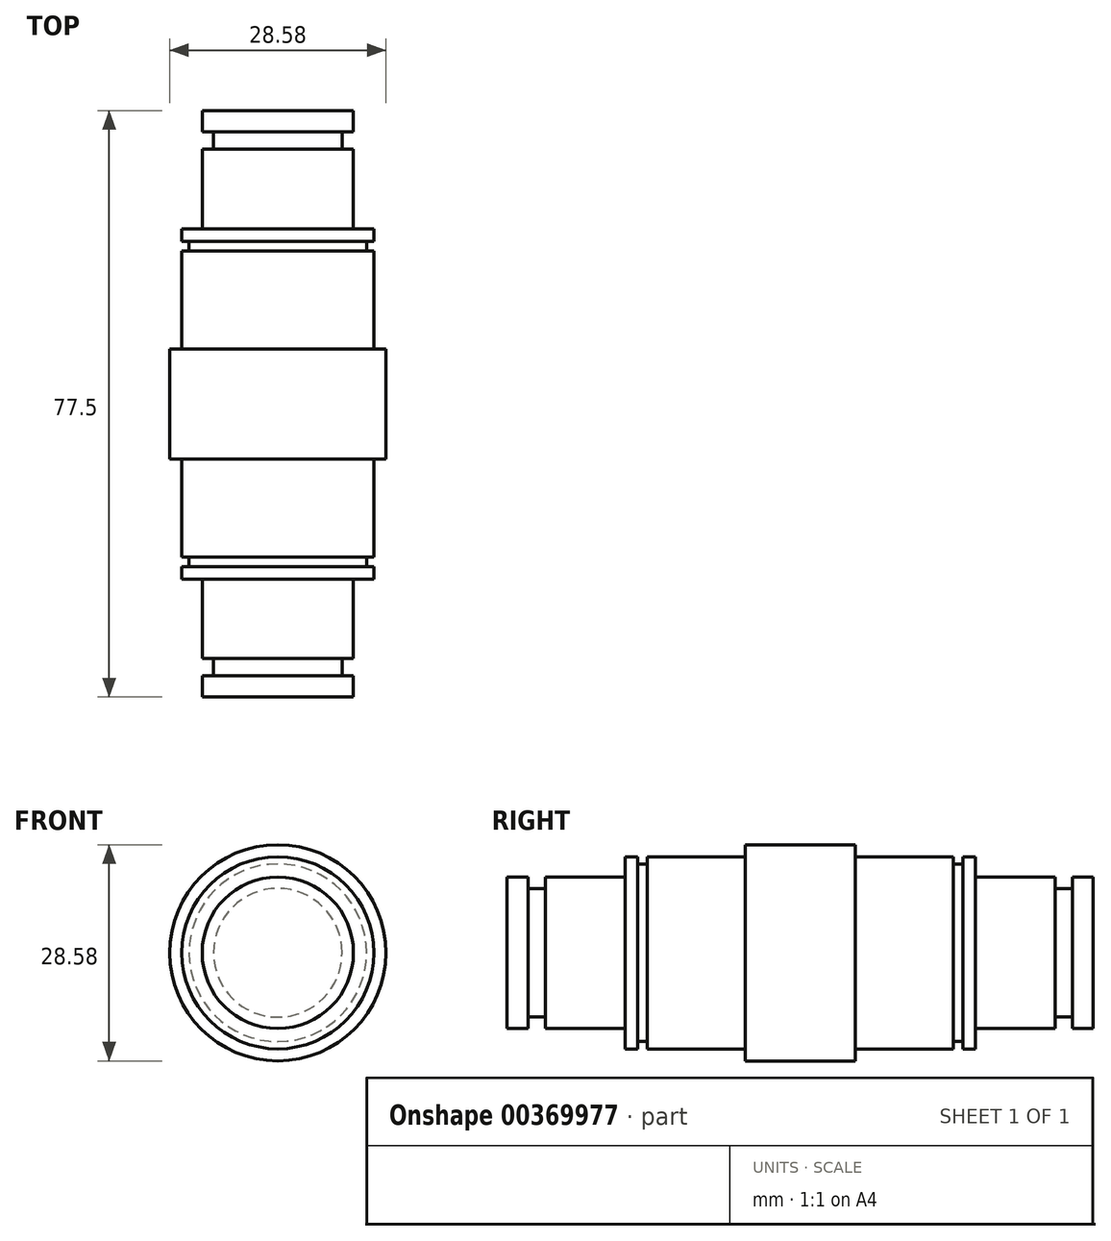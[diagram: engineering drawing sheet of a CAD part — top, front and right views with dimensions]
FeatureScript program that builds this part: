
annotation { "Feature Type Name" : "Feature", "Feature Type Description" : "" }
export const myFeature = defineFeature(function(context is Context, id is Id, definition is map)
    precondition{}
    {
        {
            var Q0;
            Q0=qCreatedBy(makeId("Right.planeOp"),FACE);
            var sketch = newSketch(context, id + "F0", { "sketchPlane" : qUnion([Q0])});
            skLineSegment(sketch, "E0", {"start": v(-30.43, 0) * mm, "end": v(-23.15, 0) * mm, "construction": true});
            skLineSegment(sketch, "E1", {"start": v(0, 0) * mm, "end": v(30.43, 0) * mm, "construction": true});
            skLineSegment(sketch, "E2.bottom", {"start": v(-38.75, 10) * mm, "end": v(-35.96, 10) * mm});
            skLineSegment(sketch, "E3", {"start": v(-38.75, 10) * mm, "end": v(-38.75, 0) * mm});
            skLineSegment(sketch, "E4.bottom", {"start": v(-23.15, 12.7) * mm, "end": v(-21.5, 12.7) * mm});
            skLineSegment(sketch, "E4.left", {"start": v(-23.15, 12.7) * mm, "end": v(-23.15, 10) * mm});
            skLineSegment(sketch, "E4.right", {"start": v(-7.28, 14.29) * mm, "end": v(-7.28, 0) * mm});
            skLineSegment(sketch, "E5.bottom", {"start": v(-7.28, 14.29) * mm, "end": v(0, 14.29) * mm});
            skLineSegment(sketch, "E6.MirrorCS", {"start": v(49.78, 0) * mm, "end": v(0, 0) * mm, "construction": true});
            skLineSegment(sketch, "E7.top", {"start": v(-35.96, 8.5) * mm, "end": v(-33.67, 8.5) * mm});
            skLineSegment(sketch, "E7.left", {"start": v(-35.96, 10) * mm, "end": v(-35.96, 8.5) * mm});
            skLineSegment(sketch, "E7.right", {"start": v(-33.67, 10) * mm, "end": v(-33.67, 8.5) * mm});
            skLineSegment(sketch, "E8.bottom", {"start": v(-21.5, 11.73) * mm, "end": v(-20.23, 11.73) * mm});
            skLineSegment(sketch, "E9", {"start": v(-21.5, 11.73) * mm, "end": v(-21.5, 12.7) * mm});
            skLineSegment(sketch, "E10", {"start": v(-20.23, 11.73) * mm, "end": v(-20.23, 12.7) * mm});
            skLineSegment(sketch, "E11.trimOffspring", {"start": v(-20.23, 12.7) * mm, "end": v(-7.28, 12.7) * mm});
            skLineSegment(sketch, "E12", {"start": v(-38.75, 0) * mm, "end": v(-23.15, 0) * mm});
            skLineSegment(sketch, "E13", {"start": v(-33.67, 10) * mm, "end": v(-23.15, 10) * mm});
            skLineSegment(sketch, "E14", {"start": v(-23.15, 10) * mm, "end": v(-23.15, 0) * mm});
            skLineSegment(sketch, "E15", {"start": v(0, 14.29) * mm, "end": v(0, 0) * mm, "construction": true});
            skLineSegment(sketch, "E16", {"start": v(-7.28, 0) * mm, "end": v(0, 0) * mm});
            skLineSegment(sketch, "E17", {"start": v(-23.15, 0) * mm, "end": v(-7.28, 0) * mm});
            skLineSegment(sketch, "E18.MirrorCS", {"start": v(30.43, 0) * mm, "end": v(23.15, 0) * mm, "construction": true});
            skLineSegment(sketch, "E19.MirrorCS", {"start": v(21.5, 11.73) * mm, "end": v(21.5, 12.7) * mm});
            skLineSegment(sketch, "E20.MirrorCS", {"start": v(35.96, 10) * mm, "end": v(35.96, 8.5) * mm});
            skLineSegment(sketch, "E21.MirrorCS", {"start": v(23.15, 12.7) * mm, "end": v(23.15, 10) * mm});
            skLineSegment(sketch, "E22.MirrorCS", {"start": v(7.28, 14.29) * mm, "end": v(7.28, 0) * mm});
            skLineSegment(sketch, "E23.MirrorCS", {"start": v(7.28, 14.29) * mm, "end": v(0, 14.29) * mm});
            skLineSegment(sketch, "E24.MirrorCS", {"start": v(7.28, 0) * mm, "end": v(0, 0) * mm});
            skLineSegment(sketch, "E25.MirrorCS", {"start": v(33.67, 10) * mm, "end": v(23.15, 10) * mm});
            skLineSegment(sketch, "E26.MirrorCS", {"start": v(38.75, 10) * mm, "end": v(38.75, 0) * mm});
            skLineSegment(sketch, "E27.MirrorCS", {"start": v(23.15, 12.7) * mm, "end": v(21.5, 12.7) * mm});
            skLineSegment(sketch, "E28.MirrorCS", {"start": v(38.75, 0) * mm, "end": v(23.15, 0) * mm});
            skLineSegment(sketch, "E29.MirrorCS", {"start": v(33.67, 10) * mm, "end": v(33.67, 8.5) * mm});
            skLineSegment(sketch, "E30.MirrorCS", {"start": v(20.23, 12.7) * mm, "end": v(7.28, 12.7) * mm});
            skLineSegment(sketch, "E31.MirrorCS", {"start": v(21.5, 11.73) * mm, "end": v(20.23, 11.73) * mm});
            skLineSegment(sketch, "E32.MirrorCS", {"start": v(23.15, 10) * mm, "end": v(23.15, 0) * mm});
            skLineSegment(sketch, "E33.MirrorCS", {"start": v(38.75, 10) * mm, "end": v(35.96, 10) * mm});
            skLineSegment(sketch, "E34.MirrorCS", {"start": v(35.96, 8.5) * mm, "end": v(33.67, 8.5) * mm});
            skLineSegment(sketch, "E35.MirrorCS", {"start": v(23.15, 0) * mm, "end": v(7.28, 0) * mm});
            skLineSegment(sketch, "E36.MirrorCS", {"start": v(20.23, 11.73) * mm, "end": v(20.23, 12.7) * mm});
            skSolve(sketch);
        }
        {
            var Q0;
            Q0=makeQuery(id+"F0.imprint","IMPRINT",FACE,{"disambiguationData":[TD([[makeQuery(id+"F0.imprint","IMPRINT",EDGE,{"derivedFrom":sQuery(id+"F0.wireOp",EDGE,"E4.bottom")}),-1.0]])]});
            var Q1;
            {var subQ1=sQuery(id+"F0.wireOp",EDGE,"E5.bottom");Q1=makeQuery(id+"F0.imprint","IMPRINT",FACE,{"disambiguationData":[TD([[makeQuery(id+"F0.imprint","IMPRINT",EDGE,{"derivedFrom":subQ1}),-1.0]])]});}
            var Q2;
            Q2=makeQuery(id+"F0.imprint","IMPRINT",FACE,{"disambiguationData":[TD([[makeQuery(id+"F0.imprint","IMPRINT",EDGE,{"derivedFrom":sQuery(id+"F0.wireOp",EDGE,"E19.MirrorCS")}),-1.0]])]});
            var Q3;
            Q3=makeQuery(id+"F0.imprint","IMPRINT",FACE,{"disambiguationData":[TD([[makeQuery(id+"F0.imprint","IMPRINT",EDGE,{"derivedFrom":sQuery(id+"F0.wireOp",EDGE,"E20.MirrorCS")}),1.0]])]});
            var Q4;
            Q4=makeQuery(id+"F0.imprint","IMPRINT",FACE,{"disambiguationData":[TD([[makeQuery(id+"F0.imprint","IMPRINT",EDGE,{"derivedFrom":sQuery(id+"F0.wireOp",EDGE,"E2.bottom")}),-1.0]])]});
            var Q5;
            Q5=sQuery(id+"F0.wireOp",EDGE,"E6.MirrorCS");
            revolve(context, id + "F1", {"entities" : qUnion([Q0, Q1, Q2, Q3, Q4]), "axis" : qUnion([Q5]), "revolveType" : RevolveType.FULL});
        }
    });
